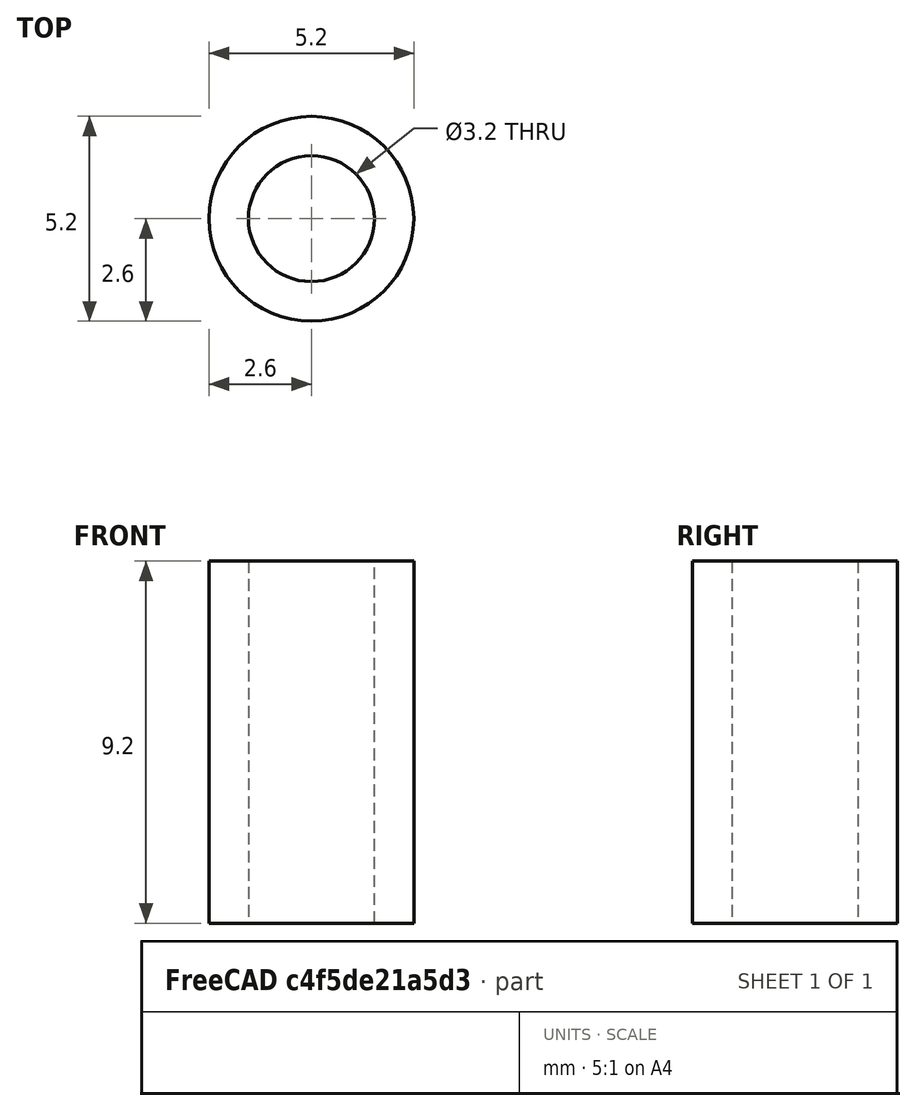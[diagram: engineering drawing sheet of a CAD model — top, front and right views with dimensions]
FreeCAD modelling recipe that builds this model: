
FCSTD DOCUMENT  (FreeCAD 0.18.1R)
Label: Tall Spacer
License: All rights reserved
LicenseURL: http://en.wikipedia.org/wiki/All_rights_reserved
objects: Sketcher::SketchObject×1, PartDesign::Pad×1, PartDesign::Body×1
note: 4 computed .brp shape members not serialized (recipe doc carries the construction recipe); baked Part::Feature solids carry a one-line shape summary decoded from their .brp

FEATURE [Sketcher::SketchObject] Sketch  label="Sketch Tall Spacer Extrude"
  MapMode = 5
  Support = -> [XY_Plane]
  sketch-geometry (2):
    g0: Circle CenterX=0 CenterY=0 CenterZ=0 NormalX=0 NormalY=0 NormalZ=1 AngleXU=0 Radius=1.6
    g1: Circle CenterX=0 CenterY=0 CenterZ=0 NormalX=0 NormalY=0 NormalZ=1 AngleXU=0 Radius=2.6
  constraints (4):
    c: Coincident(g0,g-1)
    c: Coincident(g1,g0)
    c: Diameter(g0) = 3.2
    c: Diameter(g1) = 5.2
FEATURE [PartDesign::Pad] Pad  label="Tall Spacer Extrude"
  Length = 9.2
  Length2 = 100
  Profile = -> Sketch
  Type = 0
FEATURE [PartDesign::Body] Body  label="Tall Spacer"
  Group = -> [Sketch,Pad]
  Origin = -> Origin
  Tip = -> Pad
